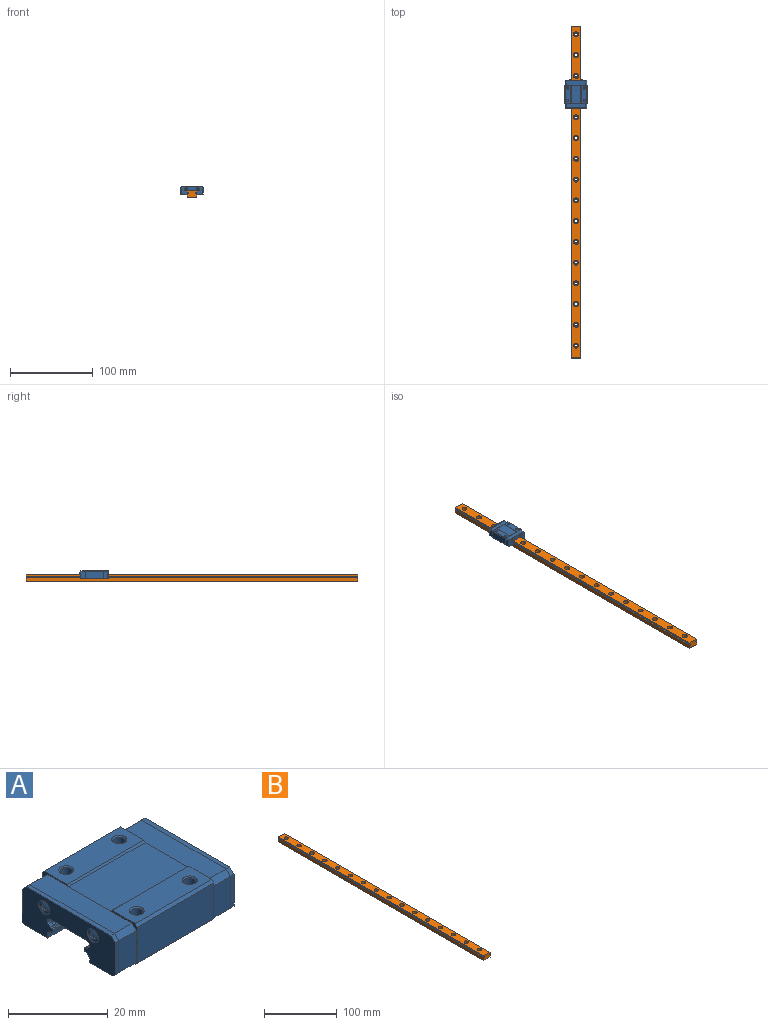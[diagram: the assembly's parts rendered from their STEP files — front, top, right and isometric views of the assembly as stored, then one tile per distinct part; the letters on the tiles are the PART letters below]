
ASSEMBLY  parts=2 mates=1
PART A: 294 faces, bbox 34.7x27x10 mm
  f0: plane 1.9x1.9mm, normal (-1,0,0), area 1.2mm2, adj f2,f3,f4,f5,f6,f7,f8,f9
  f1: plane 1.9x1.9mm, normal (-1,0,0), area 1.2mm2, adj f14,f15,f16,f17,f18,f19,f20,f21
  f2: plane 0.77x0.49mm, normal (0,1,0), area 0.3mm2, adj f0,f3,f13,f26
  f3: plane 0.77x0.49mm, normal (0,0,1), area 0.3mm2, adj f0,f2,f4,f26
  f4: plane 0.36x0.33mm, normal (0,1,0), area 0.1mm2, adj f0,f3,f5,f26
  f5: plane 0.77x0.49mm, normal (0,0,-1), area 0.3mm2, adj f0,f4,f6,f26
  f6: plane 0.77x0.49mm, normal (0,1,0), area 0.3mm2, adj f0,f5,f7,f26
  f7: plane 0.36x0.33mm, normal (0,0,-1), area 0.1mm2, adj f0,f6,f8,f26
  f8: plane 0.77x0.49mm, normal (0,-1,0), area 0.3mm2, adj f0,f7,f9,f26
  f9: plane 0.77x0.49mm, normal (0,0,-1), area 0.3mm2, adj f0,f8,f10,f26
  f10: plane 0.36x0.33mm, normal (0,-1,0), area 0.1mm2, adj f0,f9,f11,f26
  f11: plane 0.77x0.49mm, normal (0,0,1), area 0.3mm2, adj f0,f10,f12,f26
  f12: plane 0.77x0.49mm, normal (0,-1,0), area 0.3mm2, adj f0,f11,f13,f26
  f13: plane 0.36x0.33mm, normal (0,0,1), area 0.1mm2, adj f0,f2,f12,f26
  f14: plane 0.77x0.49mm, normal (0,1,0), area 0.3mm2, adj f1,f15,f25,f27
  f15: plane 0.77x0.49mm, normal (0,0,1), area 0.3mm2, adj f1,f14,f16,f27
  f16: plane 0.36x0.33mm, normal (0,1,0), area 0.1mm2, adj f1,f15,f17,f27
  f17: plane 0.77x0.49mm, normal (0,0,-1), area 0.3mm2, adj f1,f16,f18,f27
  f18: plane 0.77x0.49mm, normal (0,1,0), area 0.3mm2, adj f1,f17,f19,f27
  f19: plane 0.36x0.33mm, normal (0,0,-1), area 0.1mm2, adj f1,f18,f20,f27
  f20: plane 0.77x0.49mm, normal (0,-1,0), area 0.3mm2, adj f1,f19,f21,f27
  f21: plane 0.77x0.49mm, normal (0,0,-1), area 0.3mm2, adj f1,f20,f22,f27
  f22: plane 0.36x0.33mm, normal (0,-1,0), area 0.1mm2, adj f1,f21,f23,f27
  f23: plane 0.77x0.49mm, normal (0,0,1), area 0.3mm2, adj f1,f22,f24,f27
  f24: plane 0.77x0.49mm, normal (0,-1,0), area 0.3mm2, adj f1,f23,f25,f27
  f25: plane 0.36x0.33mm, normal (0,0,1), area 0.1mm2, adj f1,f14,f24,f27
  f26: sphere r=2.73mm, area 7.3mm2, adj f2,f3,f4,f5,f6,f7,f8,f9
  f27: sphere r=2.73mm, area 7.3mm2, adj f14,f15,f16,f17,f18,f19,f20,f21
  f28: plane 26.4x9.6mm, normal (-1,0,0), area 180.6mm2, adj f26,f27,f29,f30,f31,f32,f33,f34
  f29: plane 6.6x1mm, normal (0,0,-1), area 6.6mm2, adj f28,f30,f66,f67
  f30: plane 1x0.6mm, normal (0,-0.71,-0.71), area 0.8mm2, adj f28,f29,f31,f67
  f31: plane 7.8x1mm, normal (0,-1,0), area 7.8mm2, adj f28,f30,f32,f67
  f32: plane 1.2x1.2mm, normal (0,-0.71,0.71), area 1.7mm2, adj f28,f31,f33,f67
  f33: plane 24x1mm, normal (0,0,1), area 24mm2, adj f28,f32,f34,f67
  f34: plane 1.2x1.2mm, normal (0,0.71,0.71), area 1.7mm2, adj f28,f33,f35,f67
  f35: plane 7.8x1mm, normal (0,1,0), area 7.8mm2, adj f28,f34,f36,f67
  f36: plane 1x0.6mm, normal (0,0.71,-0.71), area 0.8mm2, adj f28,f35,f37,f67
  f37: plane 6.6x1mm, normal (0,0,-1), area 6.6mm2, adj f28,f36,f38,f67
  f38: plane 1.14x1mm, normal (0,-1,0), area 1.1mm2, adj f28,f37,f39,f67
  f39: cylinder r=0.25mm len=1mm, axis (1,0,0), area 0.3mm2, adj f28,f38,f40,f67
  f40: cylinder r=1.2mm len=1mm, axis (1,0,0), area 0.8mm2, adj f28,f39,f41,f67
  f41: cylinder r=0.25mm len=1mm, axis (1,0,0), area 0.2mm2, adj f28,f40,f42,f67
  f42: plane 1x0.35mm, normal (0,-0.09,-1), area 0.3mm2, adj f28,f41,f43,f67
  f43: cylinder r=0.25mm len=1mm, axis (1,0,0), area 0.4mm2, adj f28,f42,f44,f67
  f44: plane 1x0.45mm, normal (0,-1,0), area 0.5mm2, adj f28,f43,f45,f67
  f45: cylinder r=0.25mm len=1mm, axis (1,0,0), area 0.4mm2, adj f28,f44,f46,f67
  f46: plane 1x0.37mm, normal (0,-0.09,1), area 0.4mm2, adj f28,f45,f47,f67
  f47: cylinder r=0.25mm len=1mm, axis (1,0,0), area 0.2mm2, adj f28,f46,f48,f67
  f48: cylinder r=1.2mm len=1mm, axis (1,0,0), area 0.7mm2, adj f28,f47,f49,f67
  f49: cylinder r=0.25mm len=1mm, axis (1,0,0), area 0.3mm2, adj f28,f48,f50,f67
  f50: plane 1x0.67mm, normal (0,-1,0), area 0.7mm2, adj f28,f49,f51,f67
  f51: plane 1x0.5mm, normal (0,-0.71,-0.71), area 0.7mm2, adj f28,f50,f52,f67
  f52: plane 11x1mm, normal (0,0,-1), area 11mm2, adj f28,f51,f53,f67
  f53: plane 1x0.5mm, normal (0,0.71,-0.71), area 0.7mm2, adj f28,f52,f54,f67
  f54: plane 1x0.67mm, normal (0,1,0), area 0.7mm2, adj f28,f53,f55,f67
  f55: cylinder r=0.25mm len=1mm, axis (1,0,0), area 0.3mm2, adj f28,f54,f56,f67
  f56: cylinder r=1.2mm len=1mm, axis (1,0,0), area 0.7mm2, adj f28,f55,f57,f67
  f57: cylinder r=0.25mm len=1mm, axis (1,0,0), area 0.2mm2, adj f28,f56,f58,f67
  f58: plane 1x0.37mm, normal (0,0.09,1), area 0.4mm2, adj f28,f57,f59,f67
  f59: cylinder r=0.25mm len=1mm, axis (1,0,0), area 0.4mm2, adj f28,f58,f60,f67
  f60: plane 1x0.45mm, normal (0,1,0), area 0.5mm2, adj f28,f59,f61,f67
  f61: cylinder r=0.25mm len=1mm, axis (1,0,0), area 0.4mm2, adj f28,f60,f62,f67
  f62: plane 1x0.35mm, normal (0,0.09,-1), area 0.3mm2, adj f28,f61,f63,f67
  f63: cylinder r=0.25mm len=1mm, axis (1,0,0), area 0.2mm2, adj f28,f62,f64,f67
  f64: cylinder r=1.2mm len=1mm, axis (1,0,0), area 0.8mm2, adj f28,f63,f65,f67
  f65: cylinder r=0.25mm len=1mm, axis (1,0,0), area 0.3mm2, adj f28,f64,f66,f67
  f66: plane 1.14x1mm, normal (0,1,0), area 1.1mm2, adj f28,f29,f65,f67
  f67: plane 26.4x9.6mm, normal (1,0,0), area 171.3mm2, adj f29,f30,f31,f32,f33,f34,f35,f36
  f68: cone r=0.61mm half-angle=63.4deg, axis (0,0,1), area 5.3mm2, adj f74
  f69: cone r=0.61mm half-angle=63.4deg, axis (0,0,1), area 5.3mm2, adj f75
  f70: cone r=0.61mm half-angle=63.4deg, axis (0,0,1), area 5.3mm2, adj f76
  f71: cone r=0.61mm half-angle=63.4deg, axis (0,0,1), area 5.3mm2, adj f77
  f72: cone r=1.97mm half-angle=5deg, axis (1,0,0), area 0mm2, adj f67,f78
  f73: cone r=1.97mm half-angle=5deg, axis (1,0,0), area 0mm2, adj f67,f78
  f74: cylinder r=1.23mm len=2.46mm, axis (0,0,-1), area 6.8mm2, adj f68,f79
  f75: cylinder r=1.23mm len=2.46mm, axis (0,0,-1), area 6.8mm2, adj f69,f80
  f76: cylinder r=1.23mm len=2.46mm, axis (0,0,-1), area 6.8mm2, adj f70,f81
  f77: cylinder r=1.23mm len=2.46mm, axis (0,0,-1), area 6.8mm2, adj f71,f82
  f78: plane 26.4x9.6mm, normal (-1,0,0), area 171.3mm2, adj f72,f73,f83,f84,f85,f86,f87,f88
  f79: plane 3x3mm, normal (0,0,1), area 2.3mm2, adj f74,f121
  f80: plane 3x3mm, normal (0,0,1), area 2.3mm2, adj f75,f122
  f81: plane 3x3mm, normal (0,0,1), area 2.3mm2, adj f76,f123
  f82: plane 3x3mm, normal (0,0,1), area 2.3mm2, adj f77,f124
  f83: plane 6.6x5mm, normal (0,0,-1), area 33mm2, adj f78,f84,f120,f125
  f84: plane 5x0.6mm, normal (0,-0.71,-0.71), area 4.2mm2, adj f78,f83,f85,f125
  f85: plane 7.8x5mm, normal (0,-1,0), area 39mm2, adj f78,f84,f86,f125
  f86: plane 5x1.2mm, normal (0,-0.71,0.71), area 8.5mm2, adj f78,f85,f87,f125
  f87: plane 24x5mm, normal (0,0,1), area 120mm2, adj f78,f86,f88,f125
  f88: plane 5x1.2mm, normal (0,0.71,0.71), area 8.5mm2, adj f78,f87,f89,f125
  f89: plane 7.8x5mm, normal (0,1,0), area 39mm2, adj f78,f88,f90,f125
  f90: plane 5x0.6mm, normal (0,0.71,-0.71), area 4.2mm2, adj f78,f89,f91,f125
  f91: plane 6.6x5mm, normal (0,0,-1), area 33mm2, adj f78,f90,f92,f125
  f92: plane 5x1.14mm, normal (0,-1,0), area 5.7mm2, adj f78,f91,f93,f125
  f93: cylinder r=0.25mm len=5mm, axis (1,0,0), area 1.5mm2, adj f78,f92,f94,f125
  f94: cylinder r=1.2mm len=5mm, axis (1,0,0), area 3.9mm2, adj f78,f93,f95,f125
  f95: cylinder r=0.25mm len=5mm, axis (1,0,0), area 1.2mm2, adj f78,f94,f96,f125
  f96: plane 5x0.35mm, normal (0,-0.09,-1), area 1.7mm2, adj f78,f95,f97,f125
  f97: cylinder r=0.25mm len=5mm, axis (1,0,0), area 1.9mm2, adj f78,f96,f98,f125
  f98: plane 5x0.45mm, normal (0,-1,0), area 2.3mm2, adj f78,f97,f99,f125
  f99: cylinder r=0.25mm len=5mm, axis (1,0,0), area 1.9mm2, adj f78,f98,f100,f125
  f100: plane 5x0.37mm, normal (0,-0.09,1), area 1.8mm2, adj f78,f99,f101,f125
  f101: cylinder r=0.25mm len=5mm, axis (1,0,0), area 1.2mm2, adj f78,f100,f102,f125
  f102: cylinder r=1.2mm len=5mm, axis (1,0,0), area 3.7mm2, adj f78,f101,f103,f125
  f103: cylinder r=0.25mm len=5mm, axis (1,0,0), area 1.5mm2, adj f78,f102,f104,f125
  f104: plane 5x0.67mm, normal (0,-1,0), area 3.4mm2, adj f78,f103,f105,f125
  f105: plane 5x0.5mm, normal (0,-0.71,-0.71), area 3.5mm2, adj f78,f104,f106,f125
  f106: plane 11x5mm, normal (0,0,-1), area 55mm2, adj f78,f105,f107,f125
  f107: plane 5x0.5mm, normal (0,0.71,-0.71), area 3.5mm2, adj f78,f106,f108,f125
  f108: plane 5x0.67mm, normal (0,1,0), area 3.4mm2, adj f78,f107,f109,f125
  f109: cylinder r=0.25mm len=5mm, axis (1,0,0), area 1.5mm2, adj f78,f108,f110,f125
  f110: cylinder r=1.2mm len=5mm, axis (1,0,0), area 3.7mm2, adj f78,f109,f111,f125
  f111: cylinder r=0.25mm len=5mm, axis (1,0,0), area 1.2mm2, adj f78,f110,f112,f125
  f112: plane 5x0.37mm, normal (0,0.09,1), area 1.8mm2, adj f78,f111,f113,f125
  f113: cylinder r=0.25mm len=5mm, axis (1,0,0), area 1.9mm2, adj f78,f112,f114,f125
  f114: plane 5x0.45mm, normal (0,1,0), area 2.3mm2, adj f78,f113,f115,f125
  f115: cylinder r=0.25mm len=5mm, axis (1,0,0), area 1.9mm2, adj f78,f114,f116,f125
  f116: plane 5x0.35mm, normal (0,0.09,-1), area 1.7mm2, adj f78,f115,f117,f125
  f117: cylinder r=0.25mm len=5mm, axis (1,0,0), area 1.2mm2, adj f78,f116,f118,f125
  f118: cylinder r=1.2mm len=5mm, axis (1,0,0), area 3.9mm2, adj f78,f117,f119,f125
  f119: cylinder r=0.25mm len=5mm, axis (1,0,0), area 1.5mm2, adj f78,f118,f120,f125
  f120: plane 5x1.14mm, normal (0,1,0), area 5.7mm2, adj f78,f83,f119,f125
  f121: cone r=1.36mm half-angle=45deg, axis (0,0,-1), area 3.3mm2, adj f79,f126
  f122: cone r=1.36mm half-angle=45deg, axis (0,0,-1), area 3.3mm2, adj f80,f127
  f123: cone r=1.36mm half-angle=45deg, axis (0,0,-1), area 3.3mm2, adj f81,f128
  f124: cone r=1.36mm half-angle=45deg, axis (0,0,-1), area 3.3mm2, adj f82,f129
  f125: plane 26.4x9.6mm, normal (1,0,0), area 189.9mm2, adj f83,f84,f85,f86,f87,f88,f89,f90
  f126: cylinder r=1.23mm len=2.96mm, axis (0,0,-1), area 22.9mm2, adj f121,f132
  f127: cylinder r=1.23mm len=2.96mm, axis (0,0,-1), area 22.9mm2, adj f122,f133
  f128: cylinder r=1.23mm len=2.96mm, axis (0,0,-1), area 22.9mm2, adj f123,f134
  f129: cylinder r=1.23mm len=2.96mm, axis (0,0,-1), area 22.9mm2, adj f124,f135
  f130: cylinder r=1mm len=2mm, axis (1,0,0), area 0mm2, adj f125,f136
  f131: cylinder r=1mm len=2mm, axis (1,0,0), area 0mm2, adj f125,f136
  f132: cone r=1.36mm half-angle=45deg, axis (0,0,1), area 3.3mm2, adj f126,f141
  f133: cone r=1.36mm half-angle=45deg, axis (0,0,1), area 3.3mm2, adj f127,f141
  f134: cone r=1.36mm half-angle=45deg, axis (0,0,1), area 3.3mm2, adj f128,f145
  f135: cone r=1.36mm half-angle=45deg, axis (0,0,1), area 3.3mm2, adj f129,f145
  f136: plane 27x10mm, normal (-1,0,0), area 202.5mm2, adj f130,f131,f137,f138,f139,f140,f141,f142
  f137: plane 21.7x6.9mm, normal (0,0,-1), area 149.7mm2, adj f136,f138,f180,f183
  f138: plane 21.7x0.6mm, normal (0,-0.71,-0.71), area 18.4mm2, adj f136,f137,f139,f183
  f139: plane 21.7x8.8mm, normal (0,-1,0), area 191mm2, adj f136,f138,f140,f183
  f140: plane 21.7x0.6mm, normal (0,-0.71,0.71), area 18.4mm2, adj f136,f139,f141,f183
  f141: plane 21.7x6.5mm, normal (0,0,1), area 126.9mm2, adj f132,f133,f136,f140,f142,f183
  f142: plane 21.7x0.4mm, normal (0,0.71,0.71), area 12.3mm2, adj f136,f141,f143,f183
  f143: plane 21.7x12mm, normal (0,0,1), area 260.4mm2, adj f136,f142,f144,f183
  f144: plane 21.7x0.4mm, normal (0,-0.71,0.71), area 12.3mm2, adj f136,f143,f145,f183
  f145: plane 21.7x6.5mm, normal (0,0,1), area 126.9mm2, adj f134,f135,f136,f144,f146,f183
  f146: plane 21.7x0.6mm, normal (0,0.71,0.71), area 18.4mm2, adj f136,f145,f147,f183
  f147: plane 21.7x4.6mm, normal (0,1,0), area 99.8mm2, adj f136,f146,f148,f183
  f148: cylinder r=0.5mm len=21.7mm, axis (1,0,0), area 20.1mm2, adj f136,f147,f149,f183
  f149: plane 21.7x3.4mm, normal (0,1,0), area 73.8mm2, adj f136,f148,f150,f183
  f150: plane 21.7x0.6mm, normal (0,0.71,-0.71), area 18.4mm2, adj f136,f149,f151,f183
  f151: plane 21.7x6.9mm, normal (0,0,-1), area 149.7mm2, adj f136,f150,f152,f183
  f152: plane 21.7x1.14mm, normal (0,-1,0), area 24.8mm2, adj f136,f151,f153,f183
  f153: cylinder r=0.25mm len=21.7mm, axis (1,0,0), area 6.4mm2, adj f136,f152,f154,f183
  f154: cylinder r=1.2mm len=21.7mm, axis (1,0,0), area 16.9mm2, adj f136,f153,f155,f183
  f155: cylinder r=0.25mm len=21.7mm, axis (1,0,0), area 5.1mm2, adj f136,f154,f156,f183
  f156: plane 21.7x0.35mm, normal (0,-0.09,-1), area 7.5mm2, adj f136,f155,f157,f183
  f157: cylinder r=0.25mm len=21.7mm, axis (1,0,0), area 8mm2, adj f136,f156,f158,f183
  f158: plane 21.7x0.45mm, normal (0,-1,0), area 9.8mm2, adj f136,f157,f159,f183
  f159: cylinder r=0.25mm len=21.7mm, axis (1,0,0), area 8mm2, adj f136,f158,f160,f183
  f160: plane 21.7x0.37mm, normal (0,-0.09,1), area 8mm2, adj f136,f159,f161,f183
  f161: cylinder r=0.25mm len=21.7mm, axis (1,0,0), area 5mm2, adj f136,f160,f162,f183
  f162: cylinder r=1.2mm len=21.7mm, axis (1,0,0), area 16.1mm2, adj f136,f161,f163,f183
  f163: cylinder r=0.25mm len=21.7mm, axis (1,0,0), area 6.4mm2, adj f136,f162,f164,f183
  f164: plane 21.7x0.67mm, normal (0,-1,0), area 14.6mm2, adj f136,f163,f165,f183
  f165: plane 21.7x0.5mm, normal (0,-0.71,-0.71), area 15.3mm2, adj f136,f164,f166,f183
  f166: plane 21.7x11mm, normal (0,0,-1), area 238.7mm2, adj f136,f165,f167,f183
  f167: plane 21.7x0.5mm, normal (0,0.71,-0.71), area 15.3mm2, adj f136,f166,f168,f183
  f168: plane 21.7x0.67mm, normal (0,1,0), area 14.6mm2, adj f136,f167,f169,f183
  f169: cylinder r=0.25mm len=21.7mm, axis (1,0,0), area 6.4mm2, adj f136,f168,f170,f183
  f170: cylinder r=1.2mm len=21.7mm, axis (1,0,0), area 16.1mm2, adj f136,f169,f171,f183
  f171: cylinder r=0.25mm len=21.7mm, axis (1,0,0), area 5mm2, adj f136,f170,f172,f183
  f172: plane 21.7x0.37mm, normal (0,0.09,1), area 8mm2, adj f136,f171,f173,f183
  f173: cylinder r=0.25mm len=21.7mm, axis (1,0,0), area 8mm2, adj f136,f172,f174,f183
  f174: plane 21.7x0.45mm, normal (0,1,0), area 9.8mm2, adj f136,f173,f175,f183
  f175: cylinder r=0.25mm len=21.7mm, axis (1,0,0), area 8mm2, adj f136,f174,f176,f183
  f176: plane 21.7x0.35mm, normal (0,0.09,-1), area 7.5mm2, adj f136,f175,f177,f183
  f177: cylinder r=0.25mm len=21.7mm, axis (1,0,0), area 5.1mm2, adj f136,f176,f178,f183
  f178: cylinder r=1.2mm len=21.7mm, axis (1,0,0), area 16.9mm2, adj f136,f177,f179,f183
  f179: cylinder r=0.25mm len=21.7mm, axis (1,0,0), area 6.4mm2, adj f136,f178,f180,f183
  f180: plane 21.7x1.14mm, normal (0,1,0), area 24.8mm2, adj f136,f137,f179,f183
  f181: plane 1.9x1.9mm, normal (1,0,0), area 1.2mm2, adj f184,f185,f186,f187,f188,f189,f190,f191
  f182: plane 1.9x1.9mm, normal (1,0,0), area 1.2mm2, adj f196,f197,f198,f199,f200,f201,f202,f203
  f183: plane 27x10mm, normal (1,0,0), area 202.5mm2, adj f137,f138,f139,f140,f141,f142,f143,f144
  f184: plane 0.77x0.49mm, normal (0,1,0), area 0.3mm2, adj f181,f185,f195,f210
  f185: plane 0.77x0.49mm, normal (0,0,-1), area 0.3mm2, adj f181,f184,f186,f210
  f186: plane 0.36x0.33mm, normal (0,1,0), area 0.1mm2, adj f181,f185,f187,f210
  f187: plane 0.77x0.49mm, normal (0,0,1), area 0.3mm2, adj f181,f186,f188,f210
  f188: plane 0.77x0.49mm, normal (0,1,0), area 0.3mm2, adj f181,f187,f189,f210
  f189: plane 0.36x0.33mm, normal (0,0,1), area 0.1mm2, adj f181,f188,f190,f210
  f190: plane 0.77x0.49mm, normal (0,-1,0), area 0.3mm2, adj f181,f189,f191,f210
  f191: plane 0.77x0.49mm, normal (0,0,1), area 0.3mm2, adj f181,f190,f192,f210
  f192: plane 0.36x0.33mm, normal (0,-1,0), area 0.1mm2, adj f181,f191,f193,f210
  f193: plane 0.77x0.49mm, normal (0,0,-1), area 0.3mm2, adj f181,f192,f194,f210
  f194: plane 0.77x0.49mm, normal (0,-1,0), area 0.3mm2, adj f181,f193,f195,f210
  f195: plane 0.36x0.33mm, normal (0,0,-1), area 0.1mm2, adj f181,f184,f194,f210
  f196: plane 0.77x0.49mm, normal (0,1,0), area 0.3mm2, adj f182,f197,f207,f211
  f197: plane 0.77x0.49mm, normal (0,0,-1), area 0.3mm2, adj f182,f196,f198,f211
  f198: plane 0.36x0.33mm, normal (0,1,0), area 0.1mm2, adj f182,f197,f199,f211
  f199: plane 0.77x0.49mm, normal (0,0,1), area 0.3mm2, adj f182,f198,f200,f211
  f200: plane 0.77x0.49mm, normal (0,1,0), area 0.3mm2, adj f182,f199,f201,f211
  f201: plane 0.36x0.33mm, normal (0,0,1), area 0.1mm2, adj f182,f200,f202,f211
  f202: plane 0.77x0.49mm, normal (0,-1,0), area 0.3mm2, adj f182,f201,f203,f211
  f203: plane 0.77x0.49mm, normal (0,0,1), area 0.3mm2, adj f182,f202,f204,f211
  f204: plane 0.36x0.33mm, normal (0,-1,0), area 0.1mm2, adj f182,f203,f205,f211
  f205: plane 0.77x0.49mm, normal (0,0,-1), area 0.3mm2, adj f182,f204,f206,f211
  f206: plane 0.77x0.49mm, normal (0,-1,0), area 0.3mm2, adj f182,f205,f207,f211
  f207: plane 0.36x0.33mm, normal (0,0,-1), area 0.1mm2, adj f182,f196,f206,f211
  f208: cylinder r=1mm len=2mm, axis (-1,0,0), area 0mm2, adj f183,f212
  f209: cylinder r=1mm len=2mm, axis (-1,0,0), area 0mm2, adj f183,f212
  f210: sphere r=2.73mm, area 7.3mm2, adj f184,f185,f186,f187,f188,f189,f190,f191
  f211: sphere r=2.73mm, area 7.3mm2, adj f196,f197,f198,f199,f200,f201,f202,f203
  f212: plane 26.4x9.6mm, normal (-1,0,0), area 189.9mm2, adj f208,f209,f214,f215,f216,f217,f218,f219
  f213: plane 26.4x9.6mm, normal (1,0,0), area 180.6mm2, adj f210,f211,f252,f253,f254,f255,f256,f257
  f214: cylinder r=0.25mm len=5mm, axis (-1,0,0), area 1.5mm2, adj f212,f215,f251,f291
  f215: cylinder r=1.2mm len=5mm, axis (-1,0,0), area 3.9mm2, adj f212,f214,f216,f291
  f216: cylinder r=0.25mm len=5mm, axis (-1,0,0), area 1.2mm2, adj f212,f215,f217,f291
  f217: plane 5x0.35mm, normal (0,-0.09,-1), area 1.7mm2, adj f212,f216,f218,f291
  f218: cylinder r=0.25mm len=5mm, axis (-1,0,0), area 1.9mm2, adj f212,f217,f219,f291
  f219: plane 5x0.45mm, normal (0,-1,0), area 2.3mm2, adj f212,f218,f220,f291
  f220: cylinder r=0.25mm len=5mm, axis (-1,0,0), area 1.9mm2, adj f212,f219,f221,f291
  f221: plane 5x0.37mm, normal (0,-0.09,1), area 1.8mm2, adj f212,f220,f222,f291
  f222: cylinder r=0.25mm len=5mm, axis (-1,0,0), area 1.2mm2, adj f212,f221,f223,f291
  f223: cylinder r=1.2mm len=5mm, axis (-1,0,0), area 3.7mm2, adj f212,f222,f224,f291
  f224: cylinder r=0.25mm len=5mm, axis (-1,0,0), area 1.5mm2, adj f212,f223,f225,f291
  f225: plane 5x0.67mm, normal (0,-1,0), area 3.4mm2, adj f212,f224,f226,f291
  f226: plane 5x0.5mm, normal (0,-0.71,-0.71), area 3.5mm2, adj f212,f225,f227,f291
  f227: plane 11x5mm, normal (0,0,-1), area 55mm2, adj f212,f226,f228,f291
  f228: plane 5x0.5mm, normal (0,0.71,-0.71), area 3.5mm2, adj f212,f227,f229,f291
  f229: plane 5x0.67mm, normal (0,1,0), area 3.4mm2, adj f212,f228,f230,f291
  f230: cylinder r=0.25mm len=5mm, axis (-1,0,0), area 1.5mm2, adj f212,f229,f231,f291
  f231: cylinder r=1.2mm len=5mm, axis (-1,0,0), area 3.7mm2, adj f212,f230,f232,f291
  f232: cylinder r=0.25mm len=5mm, axis (-1,0,0), area 1.2mm2, adj f212,f231,f233,f291
  f233: plane 5x0.37mm, normal (0,0.09,1), area 1.8mm2, adj f212,f232,f234,f291
  f234: cylinder r=0.25mm len=5mm, axis (-1,0,0), area 1.9mm2, adj f212,f233,f235,f291
  f235: plane 5x0.45mm, normal (0,1,0), area 2.3mm2, adj f212,f234,f236,f291
  f236: cylinder r=0.25mm len=5mm, axis (-1,0,0), area 1.9mm2, adj f212,f235,f237,f291
  f237: plane 5x0.35mm, normal (0,0.09,-1), area 1.7mm2, adj f212,f236,f238,f291
  f238: cylinder r=0.25mm len=5mm, axis (-1,0,0), area 1.2mm2, adj f212,f237,f239,f291
  f239: cylinder r=1.2mm len=5mm, axis (-1,0,0), area 3.9mm2, adj f212,f238,f240,f291
  f240: cylinder r=0.25mm len=5mm, axis (-1,0,0), area 1.5mm2, adj f212,f239,f241,f291
  f241: plane 5x1.14mm, normal (0,1,0), area 5.7mm2, adj f212,f240,f242,f291
  f242: plane 6.6x5mm, normal (0,0,-1), area 33mm2, adj f212,f241,f243,f291
  f243: plane 5x0.6mm, normal (0,-0.71,-0.71), area 4.2mm2, adj f212,f242,f244,f291
  f244: plane 7.8x5mm, normal (0,-1,0), area 39mm2, adj f212,f243,f245,f291
  f245: plane 5x1.2mm, normal (0,-0.71,0.71), area 8.5mm2, adj f212,f244,f246,f291
  f246: plane 24x5mm, normal (0,0,1), area 120mm2, adj f212,f245,f247,f291
  f247: plane 5x1.2mm, normal (0,0.71,0.71), area 8.5mm2, adj f212,f246,f248,f291
  f248: plane 7.8x5mm, normal (0,1,0), area 39mm2, adj f212,f247,f249,f291
  f249: plane 5x0.6mm, normal (0,0.71,-0.71), area 4.2mm2, adj f212,f248,f250,f291
  f250: plane 6.6x5mm, normal (0,0,-1), area 33mm2, adj f212,f249,f251,f291
  f251: plane 5x1.14mm, normal (0,-1,0), area 5.7mm2, adj f212,f214,f250,f291
  f252: plane 6.6x1mm, normal (0,0,-1), area 6.6mm2, adj f213,f253,f289,f292
  f253: plane 1x0.6mm, normal (0,0.71,-0.71), area 0.8mm2, adj f213,f252,f254,f292
  f254: plane 7.8x1mm, normal (0,1,0), area 7.8mm2, adj f213,f253,f255,f292
  f255: plane 1.2x1.2mm, normal (0,0.71,0.71), area 1.7mm2, adj f213,f254,f256,f292
  f256: plane 24x1mm, normal (0,0,1), area 24mm2, adj f213,f255,f257,f292
  f257: plane 1.2x1.2mm, normal (0,-0.71,0.71), area 1.7mm2, adj f213,f256,f258,f292
  f258: plane 7.8x1mm, normal (0,-1,0), area 7.8mm2, adj f213,f257,f259,f292
  f259: plane 1x0.6mm, normal (0,-0.71,-0.71), area 0.8mm2, adj f213,f258,f260,f292
  f260: plane 6.6x1mm, normal (0,0,-1), area 6.6mm2, adj f213,f259,f261,f292
  f261: plane 1.14x1mm, normal (0,1,0), area 1.1mm2, adj f213,f260,f262,f292
  f262: cylinder r=0.25mm len=1mm, axis (-1,0,0), area 0.3mm2, adj f213,f261,f263,f292
  f263: cylinder r=1.2mm len=1mm, axis (-1,0,0), area 0.8mm2, adj f213,f262,f264,f292
  f264: cylinder r=0.25mm len=1mm, axis (-1,0,0), area 0.2mm2, adj f213,f263,f265,f292
  f265: plane 1x0.35mm, normal (0,0.09,-1), area 0.3mm2, adj f213,f264,f266,f292
  f266: cylinder r=0.25mm len=1mm, axis (-1,0,0), area 0.4mm2, adj f213,f265,f267,f292
  f267: plane 1x0.45mm, normal (0,1,0), area 0.5mm2, adj f213,f266,f268,f292
  f268: cylinder r=0.25mm len=1mm, axis (-1,0,0), area 0.4mm2, adj f213,f267,f269,f292
  f269: plane 1x0.37mm, normal (0,0.09,1), area 0.4mm2, adj f213,f268,f270,f292
  f270: cylinder r=0.25mm len=1mm, axis (-1,0,0), area 0.2mm2, adj f213,f269,f271,f292
  f271: cylinder r=1.2mm len=1mm, axis (-1,0,0), area 0.7mm2, adj f213,f270,f272,f292
  f272: cylinder r=0.25mm len=1mm, axis (-1,0,0), area 0.3mm2, adj f213,f271,f273,f292
  f273: plane 1x0.67mm, normal (0,1,0), area 0.7mm2, adj f213,f272,f274,f292
  f274: plane 1x0.5mm, normal (0,0.71,-0.71), area 0.7mm2, adj f213,f273,f275,f292
  f275: plane 11x1mm, normal (0,0,-1), area 11mm2, adj f213,f274,f276,f292
  f276: plane 1x0.5mm, normal (0,-0.71,-0.71), area 0.7mm2, adj f213,f275,f277,f292
  f277: plane 1x0.67mm, normal (0,-1,0), area 0.7mm2, adj f213,f276,f278,f292
  f278: cylinder r=0.25mm len=1mm, axis (-1,0,0), area 0.3mm2, adj f213,f277,f279,f292
  f279: cylinder r=1.2mm len=1mm, axis (-1,0,0), area 0.7mm2, adj f213,f278,f280,f292
  f280: cylinder r=0.25mm len=1mm, axis (-1,0,0), area 0.2mm2, adj f213,f279,f281,f292
  f281: plane 1x0.37mm, normal (0,-0.09,1), area 0.4mm2, adj f213,f280,f282,f292
  f282: cylinder r=0.25mm len=1mm, axis (-1,0,0), area 0.4mm2, adj f213,f281,f283,f292
  f283: plane 1x0.45mm, normal (0,-1,0), area 0.5mm2, adj f213,f282,f284,f292
  f284: cylinder r=0.25mm len=1mm, axis (-1,0,0), area 0.4mm2, adj f213,f283,f285,f292
  f285: plane 1x0.35mm, normal (0,-0.09,-1), area 0.3mm2, adj f213,f284,f286,f292
  f286: cylinder r=0.25mm len=1mm, axis (-1,0,0), area 0.2mm2, adj f213,f285,f287,f292
  f287: cylinder r=1.2mm len=1mm, axis (-1,0,0), area 0.8mm2, adj f213,f286,f288,f292
  f288: cylinder r=0.25mm len=1mm, axis (-1,0,0), area 0.3mm2, adj f213,f287,f289,f292
  f289: plane 1.14x1mm, normal (0,-1,0), area 1.1mm2, adj f213,f252,f288,f292
  f290: cone r=1.97mm half-angle=5deg, axis (-1,0,0), area 0mm2, adj f291,f292
  f291: plane 26.4x9.6mm, normal (1,0,0), area 171.3mm2, adj f214,f215,f216,f217,f218,f219,f220,f221
  f292: plane 26.4x9.6mm, normal (-1,0,0), area 171.3mm2, adj f252,f253,f254,f255,f256,f257,f258,f259
  f293: cone r=1.97mm half-angle=5deg, axis (-1,0,0), area 0mm2, adj f291,f292
PART B: 66 faces, bbox 12x400x8 mm
  f0: plane 400x1.51mm, normal (1,0,0), area 603.1mm2, adj f1,f15,f16,f17
  f1: plane 400x12mm, normal (0,0,1), area 4347.6mm2, adj f0,f2,f16,f17,f18,f20,f22,f24
  f2: plane 400x1.51mm, normal (-1,0,0), area 603.1mm2, adj f1,f3,f16,f17
  f3: cylinder r=1.14mm len=400mm, axis (0,1,0), area 324.2mm2, adj f2,f4,f16,f17
  f4: plane 400x0.52mm, normal (0,0,-1), area 207.6mm2, adj f3,f5,f16,f17
  f5: cylinder r=0.5mm len=400mm, axis (0,1,0), area 754.1mm2, adj f4,f6,f16,f17
  f6: plane 400x0.52mm, normal (0,0,1), area 208.9mm2, adj f5,f7,f16,f17
  f7: cylinder r=1.14mm len=400mm, axis (0,1,0), area 323.8mm2, adj f6,f8,f16,f17
  f8: plane 400x4.42mm, normal (-1,0,0), area 1767.9mm2, adj f7,f9,f16,f17
  f9: plane 400x12mm, normal (0,0,-1), area 4646.1mm2, adj f8,f10,f16,f17,f50,f51,f52,f53
  f10: plane 400x4.42mm, normal (1,0,0), area 1767.9mm2, adj f9,f11,f16,f17
  f11: cylinder r=1.14mm len=400mm, axis (0,1,0), area 323.8mm2, adj f10,f12,f16,f17
  f12: plane 400x0.52mm, normal (0,0,1), area 208.9mm2, adj f11,f13,f16,f17
  f13: cylinder r=0.5mm len=400mm, axis (0,1,0), area 754.1mm2, adj f12,f14,f16,f17
  f14: plane 400x0.52mm, normal (0,0,-1), area 207.6mm2, adj f13,f15,f16,f17
  f15: cylinder r=1.14mm len=400mm, axis (0,1,0), area 324.2mm2, adj f0,f14,f16,f17
  f16: plane 12x8mm, normal (0,-1,0), area 92.1mm2, adj f0,f1,f2,f3,f4,f5,f6,f7
  f17: plane 12x8mm, normal (0,1,0), area 92.1mm2, adj f0,f1,f2,f3,f4,f5,f6,f7
  f18: cylinder r=3mm len=6mm, axis (0,0,1), area 84.8mm2, adj f1,f19
  f19: plane 6x6mm, normal (0,0,1), area 18.7mm2, adj f18,f65
  f20: cylinder r=3mm len=6mm, axis (0,0,1), area 84.8mm2, adj f1,f21
  f21: plane 6x6mm, normal (0,0,1), area 18.7mm2, adj f20,f64
  f22: cylinder r=3mm len=6mm, axis (0,0,1), area 84.8mm2, adj f1,f23
  f23: plane 6x6mm, normal (0,0,1), area 18.7mm2, adj f22,f63
  f24: cylinder r=3mm len=6mm, axis (0,0,1), area 84.8mm2, adj f1,f25
  f25: plane 6x6mm, normal (0,0,1), area 18.7mm2, adj f24,f62
  f26: cylinder r=3mm len=6mm, axis (0,0,1), area 84.8mm2, adj f1,f27
  f27: plane 6x6mm, normal (0,0,1), area 18.7mm2, adj f26,f61
  f28: cylinder r=3mm len=6mm, axis (0,0,1), area 84.8mm2, adj f1,f29
  f29: plane 6x6mm, normal (0,0,1), area 18.7mm2, adj f28,f60
  f30: cylinder r=3mm len=6mm, axis (0,0,1), area 84.8mm2, adj f1,f31
  f31: plane 6x6mm, normal (0,0,1), area 18.7mm2, adj f30,f59
  f32: cylinder r=3mm len=6mm, axis (0,0,1), area 84.8mm2, adj f1,f33
  f33: plane 6x6mm, normal (0,0,1), area 18.7mm2, adj f32,f58
  f34: cylinder r=3mm len=6mm, axis (0,0,1), area 84.8mm2, adj f1,f35
  f35: plane 6x6mm, normal (0,0,1), area 18.7mm2, adj f34,f57
  f36: cylinder r=3mm len=6mm, axis (0,0,1), area 84.8mm2, adj f1,f37
  f37: plane 6x6mm, normal (0,0,1), area 18.7mm2, adj f36,f56
  f38: cylinder r=3mm len=6mm, axis (0,0,1), area 84.8mm2, adj f1,f39
  f39: plane 6x6mm, normal (0,0,1), area 18.7mm2, adj f38,f55
  f40: cylinder r=3mm len=6mm, axis (0,0,1), area 84.8mm2, adj f1,f41
  f41: plane 6x6mm, normal (0,0,1), area 18.7mm2, adj f40,f54
  f42: cylinder r=3mm len=6mm, axis (0,0,1), area 84.8mm2, adj f1,f43
  f43: plane 6x6mm, normal (0,0,1), area 18.7mm2, adj f42,f53
  f44: cylinder r=3mm len=6mm, axis (0,0,1), area 84.8mm2, adj f1,f45
  f45: plane 6x6mm, normal (0,0,1), area 18.7mm2, adj f44,f52
  f46: plane 6x6mm, normal (0,0,1), area 18.7mm2, adj f47,f51
  f47: cylinder r=3mm len=6mm, axis (0,0,1), area 84.8mm2, adj f1,f46
  f48: cylinder r=3mm len=6mm, axis (0,0,1), area 84.8mm2, adj f1,f49
  f49: plane 6x6mm, normal (0,0,1), area 18.7mm2, adj f48,f50
  f50: cylinder r=1.75mm len=3.5mm, axis (0,0,1), area 38.5mm2, adj f9,f49
  f51: cylinder r=1.75mm len=3.5mm, axis (0,0,1), area 38.5mm2, adj f9,f46
  f52: cylinder r=1.75mm len=3.5mm, axis (0,0,1), area 38.5mm2, adj f9,f45
  f53: cylinder r=1.75mm len=3.5mm, axis (0,0,1), area 38.5mm2, adj f9,f43
  f54: cylinder r=1.75mm len=3.5mm, axis (0,0,1), area 38.5mm2, adj f9,f41
  f55: cylinder r=1.75mm len=3.5mm, axis (0,0,1), area 38.5mm2, adj f9,f39
  f56: cylinder r=1.75mm len=3.5mm, axis (0,0,1), area 38.5mm2, adj f9,f37
  f57: cylinder r=1.75mm len=3.5mm, axis (0,0,1), area 38.5mm2, adj f9,f35
  f58: cylinder r=1.75mm len=3.5mm, axis (0,0,1), area 38.5mm2, adj f9,f33
  f59: cylinder r=1.75mm len=3.5mm, axis (0,0,1), area 38.5mm2, adj f9,f31
  f60: cylinder r=1.75mm len=3.5mm, axis (0,0,1), area 38.5mm2, adj f9,f29
  f61: cylinder r=1.75mm len=3.5mm, axis (0,0,1), area 38.5mm2, adj f9,f27
  f62: cylinder r=1.75mm len=3.5mm, axis (0,0,1), area 38.5mm2, adj f9,f25
  f63: cylinder r=1.75mm len=3.5mm, axis (0,0,1), area 38.5mm2, adj f9,f23
  f64: cylinder r=1.75mm len=3.5mm, axis (0,0,1), area 38.5mm2, adj f9,f21
  f65: cylinder r=1.75mm len=3.5mm, axis (0,0,1), area 38.5mm2, adj f9,f19
PLACE A rot(axis=(0,0,-1),90deg) t=(-4.62,41.26,14.58)mm
PLACE B t=(1.38,0,14.58)mm fixed
MATE slider A.f28 <-> B.f17  axis (0,1,0) through (-4.62,-65.22,22.58)mm
